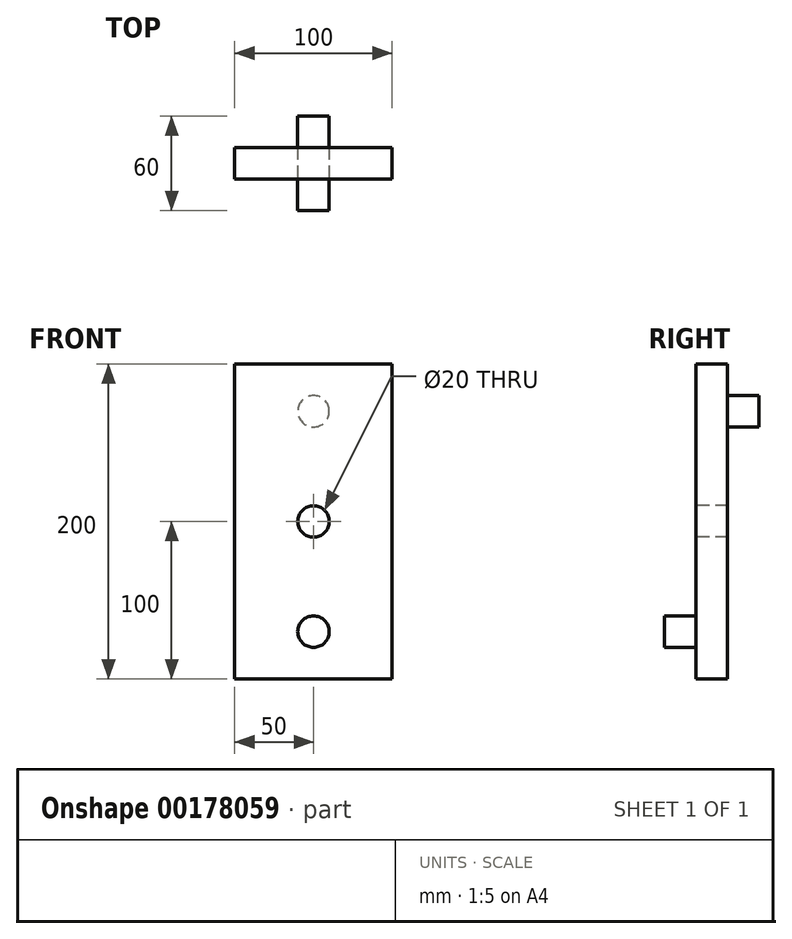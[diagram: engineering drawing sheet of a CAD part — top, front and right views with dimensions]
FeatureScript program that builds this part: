
annotation { "Feature Type Name" : "Feature", "Feature Type Description" : "" }
export const myFeature = defineFeature(function(context is Context, id is Id, definition is map)
    precondition{}
    {
        {
            var Q0;
            Q0=qCreatedBy(makeId("Front.planeOp"),FACE);
            var sketch = newSketch(context, id + "F0", { "sketchPlane" : qUnion([Q0])});
            skLineSegment(sketch, "E0.bottom", {"start": v(50, 100) * mm, "end": v(-50, 100) * mm});
            skLineSegment(sketch, "E0.top", {"start": v(50, -100) * mm, "end": v(-50, -100) * mm});
            skLineSegment(sketch, "E0.left", {"start": v(50, 100) * mm, "end": v(50, -100) * mm});
            skLineSegment(sketch, "E0.right", {"start": v(-50, 100) * mm, "end": v(-50, -100) * mm});
            skPoint(sketch, "E0.middle", {"position": v(0, 0) * mm});
            skSolve(sketch);
        }
        {
            var Q0;
            Q0 = qSketchRegion(id + "F0", true);
            extrude(context, id + "F1", {"entities" : qUnion([Q0]), "depth" : 20 * mm});
        }
        {
            var Q0;
            Q0=makeQuery(id+"F1.opExtrude","CAP_FACE",FACE,{"disambiguationData":[OSD([sQuery(id+"F0.wireOp",EDGE,"E0.bottom"),sQuery(id+"F0.wireOp",EDGE,"E0.top"),sQuery(id+"F0.wireOp",EDGE,"E0.left"),sQuery(id+"F0.wireOp",EDGE,"E0.right")])],"isStart":false});
            var sketch = newSketch(context, id + "F2", { "sketchPlane" : qUnion([Q0])});
            skCircle(sketch, "E1", {"center": v(0, 0) * mm, "radius": 10 * mm});
            skSolve(sketch);
        }
        {
            var Q0;
            Q0 = qSketchRegion(id + "F2", true);
            extrude(context, id + "F3", {"entities" : qUnion([Q0]), "operationType" : NewBodyOperationType.REMOVE, "endBound" : BoundingType.THROUGH_ALL, "oppositeDirection" : true, "depth" : 25 * mm});
        }
        {
            var Q0;
            Q0=makeQuery(id+"F1.opExtrude","CAP_FACE",FACE,{"disambiguationData":[OSD([sQuery(id+"F0.wireOp",EDGE,"E0.bottom"),sQuery(id+"F0.wireOp",EDGE,"E0.top"),sQuery(id+"F0.wireOp",EDGE,"E0.left"),sQuery(id+"F0.wireOp",EDGE,"E0.right")])],"isStart":false});
            var sketch = newSketch(context, id + "F4", { "sketchPlane" : qUnion([Q0])});
            skCircle(sketch, "E2", {"center": v(0, -70) * mm, "radius": 10 * mm});
            skSolve(sketch);
        }
        {
            var Q0;
            Q0 = qSketchRegion(id + "F4", true);
            extrude(context, id + "F5", {"entities" : qUnion([Q0]), "operationType" : NewBodyOperationType.ADD, "depth" : 20 * mm});
        }
        {
            var Q0;
            Q0=makeQuery(id+"F1.opExtrude","CAP_FACE",FACE,{"disambiguationData":[OSD([sQuery(id+"F0.wireOp",EDGE,"E0.bottom"),sQuery(id+"F0.wireOp",EDGE,"E0.top"),sQuery(id+"F0.wireOp",EDGE,"E0.left"),sQuery(id+"F0.wireOp",EDGE,"E0.right")])],"isStart":true});
            var sketch = newSketch(context, id + "F6", { "sketchPlane" : qUnion([Q0])});
            skCircle(sketch, "E3", {"center": v(0, 70) * mm, "radius": 10 * mm});
            skSolve(sketch);
        }
        {
            var Q0;
            Q0 = qSketchRegion(id + "F6", true);
            extrude(context, id + "F7", {"entities" : qUnion([Q0]), "operationType" : NewBodyOperationType.ADD, "depth" : 20 * mm});
        }
    });
